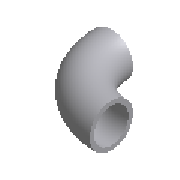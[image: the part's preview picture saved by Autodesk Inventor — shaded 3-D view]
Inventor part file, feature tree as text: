
AUTODESK INVENTOR PART (.ipt)
format: ipt  version: 2025.1 (Build 291241020, 241B)  size: 184,320 bytes
history: native  units: mm (DEFAULTED — no unit token found)
features: other x4, sweep x1
ambient origin geometry x8: Origin, YZ Plane, XZ Plane, XY Plane, X Axis, Y Axis, Z Axis, Center Point
bodies: Solid1 (feature_tree)
feature tree (5):
  sweep  "Sweep1"
  other  "Work Point1"
  other  "Work Point2"
  other  "Work Axis1"
  other  "Work Axis2"
